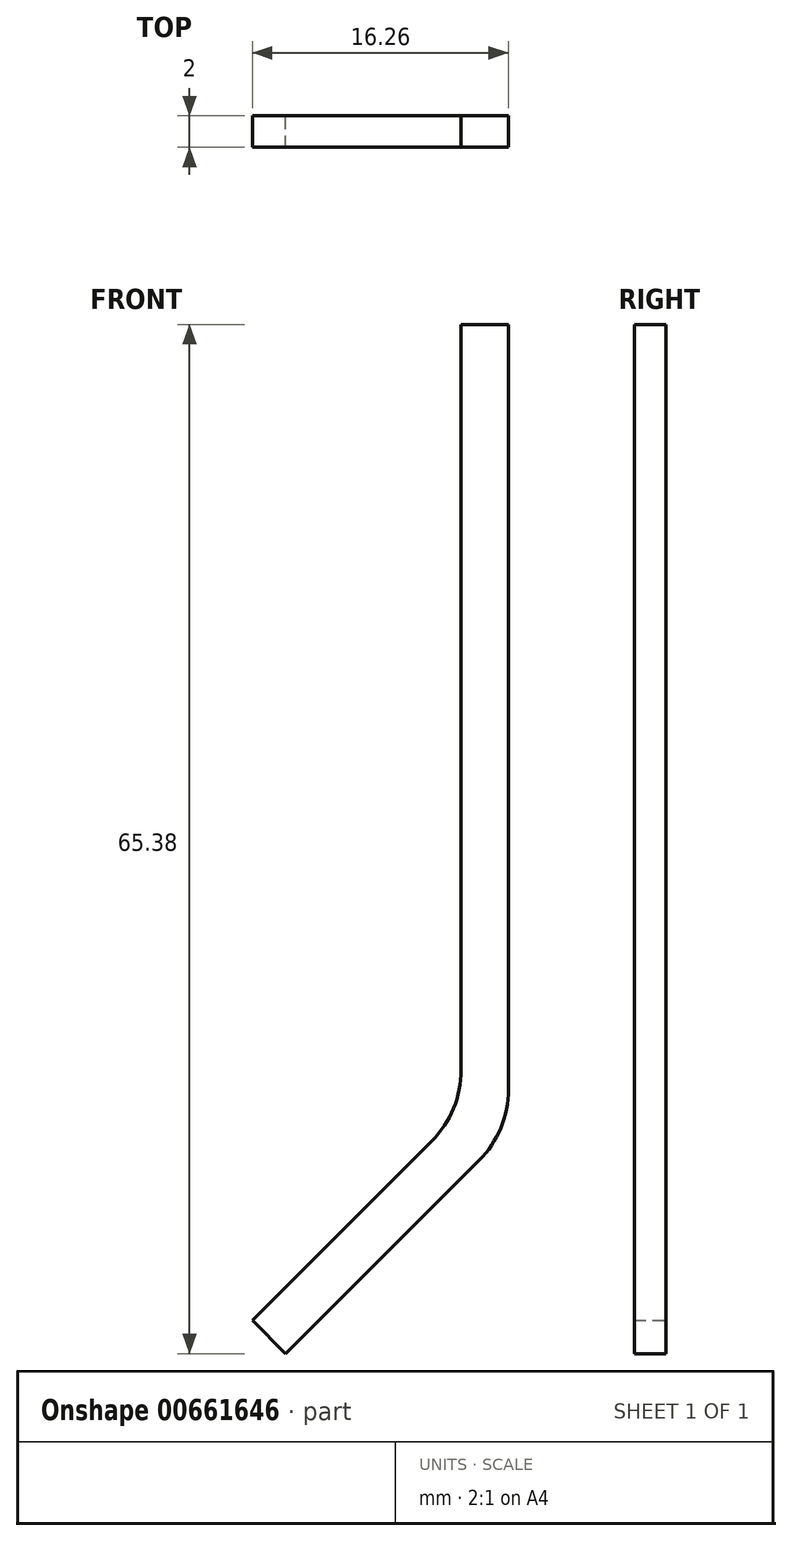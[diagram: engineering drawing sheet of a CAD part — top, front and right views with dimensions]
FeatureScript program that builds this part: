
annotation { "Feature Type Name" : "Feature", "Feature Type Description" : "" }
export const myFeature = defineFeature(function(context is Context, id is Id, definition is map)
    precondition{}
    {
        {
            var Q0;
            Q0=qCreatedBy(makeId("Front.planeOp"),FACE);
            var sketch = newSketch(context, id + "F0", { "sketchPlane" : qUnion([Q0])});
            skLineSegment(sketch, "E0", {"start": v(0, 2.63) * mm, "end": v(0, 51.24) * mm});
            skLineSegment(sketch, "E1", {"start": v(0, 51.24) * mm, "end": v(-3, 51.24) * mm});
            skLineSegment(sketch, "E2", {"start": v(-3, 51.24) * mm, "end": v(-3, 3.87) * mm});
            skLineSegment(sketch, "E3", {"start": v(-4.86, -0.62) * mm, "end": v(-16.26, -12.02) * mm});
            skLineSegment(sketch, "E4", {"start": v(-16.26, -12.02) * mm, "end": v(-14.14, -14.14) * mm});
            skLineSegment(sketch, "E5", {"start": v(-14.14, -14.14) * mm, "end": v(-1.86, -1.86) * mm});
            skPoint(sketch, "E6.visualSharp", {"position": v(-3, 1.24) * mm});
            skArc(sketch, "E6.filletArc", {"start": v(-4.86, -0.62) * mm, "mid": v(-3.48, 1.44) * mm, "end": v(-3, 3.87) * mm});
            skPoint(sketch, "E7.visualSharp", {"position": v(0, 0) * mm});
            skArc(sketch, "E7.filletArc", {"start": v(-1.86, -1.86) * mm, "mid": v(-0.48, 0.2) * mm, "end": v(0, 2.63) * mm});
            skSolve(sketch);
        }
        {
            var Q0;
            Q0 = qSketchRegion(id + "F0", true);
            extrude(context, id + "F1", {"entities" : qUnion([Q0]), "endBound" : BoundingType.SYMMETRIC, "depth" : 2 * mm, "offsetDistance" : 25.4 * mm});
        }
    });
